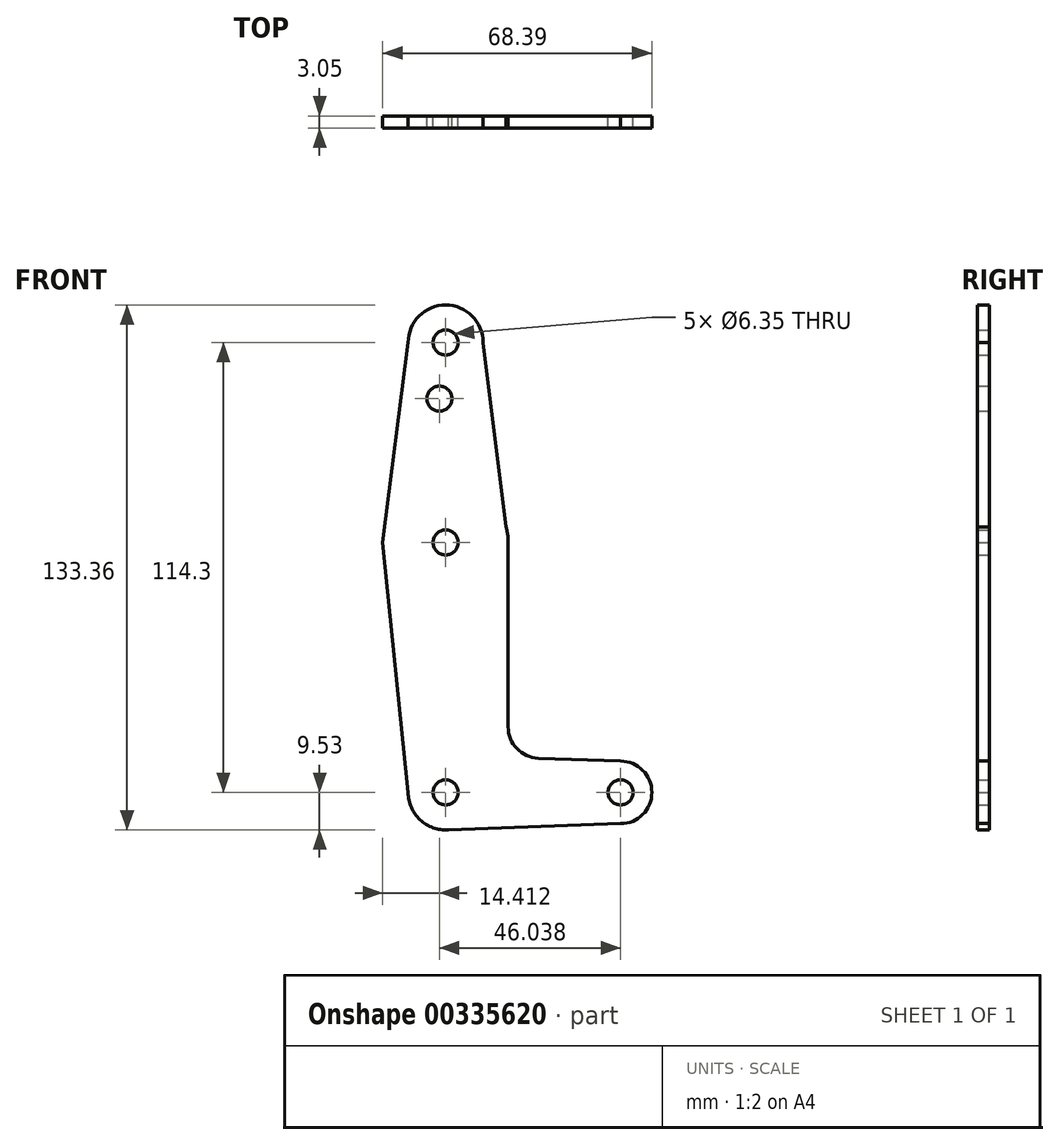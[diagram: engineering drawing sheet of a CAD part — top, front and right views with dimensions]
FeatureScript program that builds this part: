
annotation { "Feature Type Name" : "Feature", "Feature Type Description" : "" }
export const myFeature = defineFeature(function(context is Context, id is Id, definition is map)
    precondition{}
    {
        {
            var Q0;
            Q0=qCreatedBy(makeId("Front.planeOp"),FACE);
            var sketch = newSketch(context, id + "F0", { "sketchPlane" : qUnion([Q0])});
            skLineSegment(sketch, "E0", {"start": v(0, 0) * mm, "end": v(0, 114.3) * mm, "construction": true});
            skLineSegment(sketch, "E1", {"start": v(0, 0) * mm, "end": v(44.45, 0) * mm, "construction": true});
            skCircle(sketch, "E2", {"center": v(0, 0) * mm, "radius": 9.53 * mm});
            skCircle(sketch, "E3", {"center": v(44.45, 0) * mm, "radius": 7.94 * mm});
            skCircle(sketch, "E4", {"center": v(0, 63.5) * mm, "radius": 15.88 * mm});
            skCircle(sketch, "E5", {"center": v(0, 114.3) * mm, "radius": 9.53 * mm});
            skLineSegment(sketch, "E6", {"start": v(-9.53, 114.3) * mm, "end": v(-16, 63.5) * mm});
            skLineSegment(sketch, "E7", {"start": v(9.52, 114.3) * mm, "end": v(15.88, 63.5) * mm});
            skLineSegment(sketch, "E8", {"start": v(-16, 63.5) * mm, "end": v(-9.52, 0) * mm});
            skLineSegment(sketch, "E9", {"start": v(15.88, 63.5) * mm, "end": v(15.88, 16.63) * mm});
            skLineSegment(sketch, "E10", {"start": v(44.45, 7.94) * mm, "end": v(23.54, 8.69) * mm});
            skLineSegment(sketch, "E11", {"start": v(44.45, -7.94) * mm, "end": v(0, -9.53) * mm});
            skCircle(sketch, "E12", {"center": v(0, 114.3) * mm, "radius": 3.18 * mm});
            skCircle(sketch, "E13", {"center": v(-1.59, 100.03) * mm, "radius": 3.18 * mm});
            skCircle(sketch, "E14", {"center": v(0, 63.5) * mm, "radius": 3.18 * mm});
            skCircle(sketch, "E15", {"center": v(0, 0) * mm, "radius": 3.18 * mm});
            skCircle(sketch, "E16", {"center": v(44.45, 0) * mm, "radius": 3.18 * mm});
            skPoint(sketch, "E17.newPointA", {"position": v(0, 9.53) * mm});
            skArc(sketch, "E17.filletArc", {"start": v(15.88, 16.63) * mm, "mid": v(18.1, 11.11) * mm, "end": v(23.54, 8.69) * mm});
            skSolve(sketch);
        }
        {
            var Q0;
            Q0 = qSketchRegion(id + "F0", true);
            extrude(context, id + "F1", {"entities" : qUnion([Q0]), "depth" : 3.05 * mm});
        }
    });
